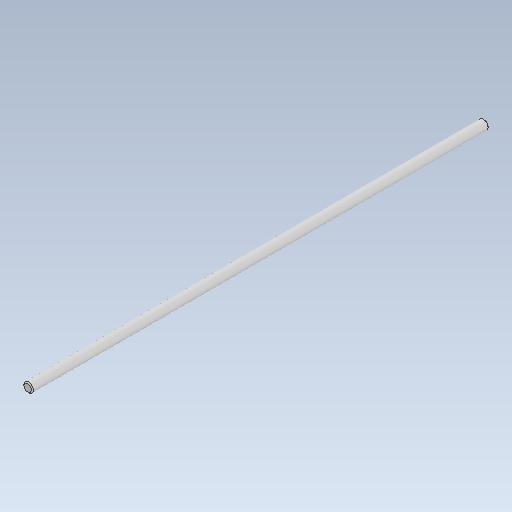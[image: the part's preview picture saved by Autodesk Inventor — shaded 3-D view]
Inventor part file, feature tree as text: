
AUTODESK INVENTOR PART (.ipt)
format: ipt  version: 2020 (Build 240168000, 168)  size: 84,480 bytes
history: native  units: in
note: dims shown in document units (in); Inventor stores cm internally (conversion verified against a paired STEP export)
features: chamfer x1
ambient origin geometry x8: Origin, YZ Plane, XZ Plane, XY Plane, X Axis, Y Axis, Z Axis, Center Point
bodies: Solid1 (feature_tree)
feature tree (1):
  chamfer  "Chamfer1"  [1 undecoded]
note: 1 required parameter value undecoded (feature->parameter linkage not recoverable at this tier; creation-order binding heuristic only, values carry confidence <= 0.55)
